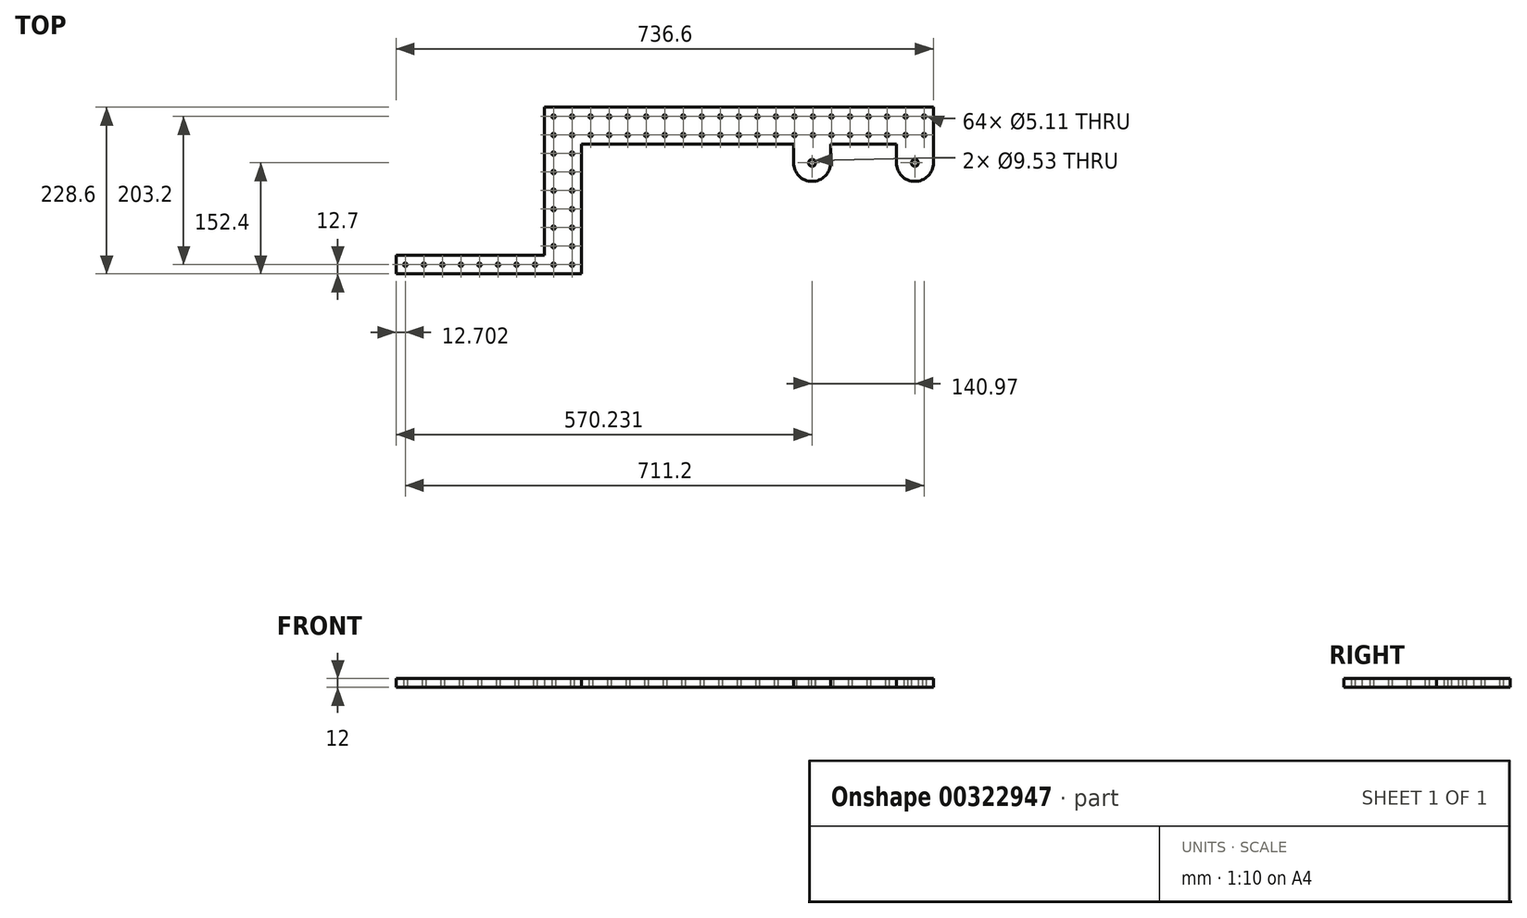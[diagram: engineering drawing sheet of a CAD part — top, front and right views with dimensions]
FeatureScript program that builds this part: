
annotation { "Feature Type Name" : "Feature", "Feature Type Description" : "" }
export const myFeature = defineFeature(function(context is Context, id is Id, definition is map)
    precondition{}
    {
        {
            var Q0;
            Q0=qCreatedBy(makeId("Top.planeOp"),FACE);
            var sketch = newSketch(context, id + "F0", { "sketchPlane" : qUnion([Q0])});
            skLineSegment(sketch, "E0", {"start": v(-259.3, 50.8) * mm, "end": v(274.1, 50.8) * mm});
            skLineSegment(sketch, "E1", {"start": v(274.1, 50.8) * mm, "end": v(274.1, 0) * mm});
            skLineSegment(sketch, "E2", {"start": v(-208.5, -177.8) * mm, "end": v(-208.5, 0) * mm});
            skLineSegment(sketch, "E3", {"start": v(-208.5, 0) * mm, "end": v(82.32, 0) * mm});
            skLineSegment(sketch, "E4", {"start": v(82.32, -25.4) * mm, "end": v(271.56, -25.4) * mm, "construction": true});
            skLineSegment(sketch, "E5", {"start": v(133.12, -25.4) * mm, "end": v(133.12, 0) * mm});
            skLineSegment(sketch, "E6", {"start": v(274.1, 0) * mm, "end": v(274.1, -25.4) * mm});
            skLineSegment(sketch, "E7", {"start": v(223.3, 0) * mm, "end": v(223.3, -25.4) * mm});
            skArc(sketch, "E8", {"start": v(223.3, -25.4) * mm, "mid": v(248.7, -50.8) * mm, "end": v(274.1, -25.4) * mm});
            skLineSegment(sketch, "E9", {"start": v(82.32, 0) * mm, "end": v(82.32, -25.4) * mm});
            skArc(sketch, "E10", {"start": v(82.32, -25.4) * mm, "mid": v(107.72, -50.8) * mm, "end": v(133.12, -25.4) * mm});
            skLineSegment(sketch, "E11", {"start": v(133.12, 0) * mm, "end": v(223.3, 0) * mm});
            skCircle(sketch, "E12", {"center": v(107.72, -25.4) * mm, "radius": 4.76 * mm});
            skCircle(sketch, "E13", {"center": v(248.7, -25.4) * mm, "radius": 4.76 * mm});
            skLineSegment(sketch, "E14", {"start": v(-259.3, 50.8) * mm, "end": v(-259.3, -152.4) * mm});
            skLineSegment(sketch, "E15", {"start": v(-259.3, -152.4) * mm, "end": v(-462.5, -152.4) * mm});
            skLineSegment(sketch, "E16", {"start": v(-462.5, -152.4) * mm, "end": v(-462.5, -177.8) * mm});
            skLineSegment(sketch, "E17", {"start": v(-462.5, -177.8) * mm, "end": v(-208.5, -177.8) * mm});
            skCircle(sketch, "E18", {"center": v(-449.8, -165.1) * mm, "radius": 2.55 * mm});
            skPoint(sketch, "E18.centerSnap0", {"position": v(-462.5, -165.1) * mm});
            skCircle(sketch, "E19.1.0.0", {"center": v(-424.4, -165.1) * mm, "radius": 2.55 * mm});
            skCircle(sketch, "E19.2.0.0", {"center": v(-399, -165.1) * mm, "radius": 2.55 * mm});
            skCircle(sketch, "E19.3.0.0", {"center": v(-373.6, -165.1) * mm, "radius": 2.55 * mm});
            skCircle(sketch, "E19.4.0.0", {"center": v(-348.2, -165.1) * mm, "radius": 2.55 * mm});
            skCircle(sketch, "E19.5.0.0", {"center": v(-322.8, -165.1) * mm, "radius": 2.55 * mm});
            skCircle(sketch, "E19.6.0.0", {"center": v(-297.4, -165.1) * mm, "radius": 2.55 * mm});
            skCircle(sketch, "E19.7.0.0", {"center": v(-272, -165.1) * mm, "radius": 2.55 * mm});
            skLineSegment(sketch, "E19.direction1", {"start": v(-449.8, -165.1) * mm, "end": v(-424.4, -165.1) * mm, "construction": true});
            skCircle(sketch, "E20", {"center": v(-246.6, -165.1) * mm, "radius": 2.55 * mm});
            skCircle(sketch, "E21.0.1.0", {"center": v(-246.6, -139.7) * mm, "radius": 2.55 * mm});
            skCircle(sketch, "E21.0.2.0", {"center": v(-246.6, -114.3) * mm, "radius": 2.55 * mm});
            skCircle(sketch, "E21.0.3.0", {"center": v(-246.6, -88.9) * mm, "radius": 2.55 * mm});
            skCircle(sketch, "E21.0.4.0", {"center": v(-246.6, -63.5) * mm, "radius": 2.55 * mm});
            skCircle(sketch, "E21.0.5.0", {"center": v(-246.6, -38.1) * mm, "radius": 2.55 * mm});
            skCircle(sketch, "E21.0.6.0", {"center": v(-246.6, -12.7) * mm, "radius": 2.55 * mm});
            skCircle(sketch, "E21.0.7.0", {"center": v(-246.6, 12.7) * mm, "radius": 2.55 * mm});
            skCircle(sketch, "E21.0.8.0", {"center": v(-246.6, 38.1) * mm, "radius": 2.55 * mm});
            skCircle(sketch, "E21.1.0.0", {"center": v(-221.2, -165.1) * mm, "radius": 2.55 * mm});
            skCircle(sketch, "E21.1.1.0", {"center": v(-221.2, -139.7) * mm, "radius": 2.55 * mm});
            skCircle(sketch, "E21.1.2.0", {"center": v(-221.2, -114.3) * mm, "radius": 2.55 * mm});
            skCircle(sketch, "E21.1.3.0", {"center": v(-221.2, -88.9) * mm, "radius": 2.55 * mm});
            skCircle(sketch, "E21.1.4.0", {"center": v(-221.2, -63.5) * mm, "radius": 2.55 * mm});
            skCircle(sketch, "E21.1.5.0", {"center": v(-221.2, -38.1) * mm, "radius": 2.55 * mm});
            skCircle(sketch, "E21.1.6.0", {"center": v(-221.2, -12.7) * mm, "radius": 2.55 * mm});
            skCircle(sketch, "E21.1.7.0", {"center": v(-221.2, 12.7) * mm, "radius": 2.55 * mm});
            skCircle(sketch, "E21.1.8.0", {"center": v(-221.2, 38.1) * mm, "radius": 2.55 * mm});
            skLineSegment(sketch, "E21.direction1", {"start": v(-246.6, -165.1) * mm, "end": v(-221.2, -165.1) * mm, "construction": true});
            skLineSegment(sketch, "E21.direction2", {"start": v(-246.6, -165.1) * mm, "end": v(-246.6, -139.7) * mm, "construction": true});
            skLineSegment(sketch, "E22", {"start": v(-208.5, 0) * mm, "end": v(-208.5, 50.8) * mm, "construction": true});
            skCircle(sketch, "E23", {"center": v(-195.8, 12.7) * mm, "radius": 2.55 * mm});
            skCircle(sketch, "E24.0.1.0", {"center": v(-195.8, 38.1) * mm, "radius": 2.55 * mm});
            skCircle(sketch, "E24.1.0.0", {"center": v(-170.4, 12.7) * mm, "radius": 2.55 * mm});
            skCircle(sketch, "E24.1.1.0", {"center": v(-170.4, 38.1) * mm, "radius": 2.55 * mm});
            skCircle(sketch, "E24.2.0.0", {"center": v(-145, 12.7) * mm, "radius": 2.55 * mm});
            skCircle(sketch, "E24.2.1.0", {"center": v(-145, 38.1) * mm, "radius": 2.55 * mm});
            skCircle(sketch, "E24.3.0.0", {"center": v(-119.6, 12.7) * mm, "radius": 2.55 * mm});
            skCircle(sketch, "E24.3.1.0", {"center": v(-119.6, 38.1) * mm, "radius": 2.55 * mm});
            skCircle(sketch, "E24.4.0.0", {"center": v(-94.2, 12.7) * mm, "radius": 2.55 * mm});
            skCircle(sketch, "E24.4.1.0", {"center": v(-94.2, 38.1) * mm, "radius": 2.55 * mm});
            skCircle(sketch, "E24.5.0.0", {"center": v(-68.8, 12.7) * mm, "radius": 2.55 * mm});
            skCircle(sketch, "E24.5.1.0", {"center": v(-68.8, 38.1) * mm, "radius": 2.55 * mm});
            skCircle(sketch, "E24.6.0.0", {"center": v(-43.4, 12.7) * mm, "radius": 2.55 * mm});
            skCircle(sketch, "E24.6.1.0", {"center": v(-43.4, 38.1) * mm, "radius": 2.55 * mm});
            skCircle(sketch, "E24.7.0.0", {"center": v(-18, 12.7) * mm, "radius": 2.55 * mm});
            skCircle(sketch, "E24.7.1.0", {"center": v(-18, 38.1) * mm, "radius": 2.55 * mm});
            skCircle(sketch, "E24.8.0.0", {"center": v(7.4, 12.7) * mm, "radius": 2.55 * mm});
            skCircle(sketch, "E24.8.1.0", {"center": v(7.4, 38.1) * mm, "radius": 2.55 * mm});
            skCircle(sketch, "E24.9.0.0", {"center": v(32.8, 12.7) * mm, "radius": 2.55 * mm});
            skCircle(sketch, "E24.9.1.0", {"center": v(32.8, 38.1) * mm, "radius": 2.55 * mm});
            skCircle(sketch, "E24.10.0.0", {"center": v(58.2, 12.7) * mm, "radius": 2.55 * mm});
            skCircle(sketch, "E24.10.1.0", {"center": v(58.2, 38.1) * mm, "radius": 2.55 * mm});
            skCircle(sketch, "E24.11.0.0", {"center": v(83.6, 12.7) * mm, "radius": 2.55 * mm});
            skCircle(sketch, "E24.11.1.0", {"center": v(83.6, 38.1) * mm, "radius": 2.55 * mm});
            skCircle(sketch, "E24.12.0.0", {"center": v(109, 12.7) * mm, "radius": 2.55 * mm});
            skCircle(sketch, "E24.12.1.0", {"center": v(109, 38.1) * mm, "radius": 2.55 * mm});
            skCircle(sketch, "E24.13.0.0", {"center": v(134.4, 12.7) * mm, "radius": 2.55 * mm});
            skCircle(sketch, "E24.13.1.0", {"center": v(134.4, 38.1) * mm, "radius": 2.55 * mm});
            skCircle(sketch, "E24.14.0.0", {"center": v(159.8, 12.7) * mm, "radius": 2.55 * mm});
            skCircle(sketch, "E24.14.1.0", {"center": v(159.8, 38.1) * mm, "radius": 2.55 * mm});
            skCircle(sketch, "E24.15.0.0", {"center": v(185.2, 12.7) * mm, "radius": 2.55 * mm});
            skCircle(sketch, "E24.15.1.0", {"center": v(185.2, 38.1) * mm, "radius": 2.55 * mm});
            skCircle(sketch, "E24.16.0.0", {"center": v(210.6, 12.7) * mm, "radius": 2.55 * mm});
            skCircle(sketch, "E24.16.1.0", {"center": v(210.6, 38.1) * mm, "radius": 2.55 * mm});
            skCircle(sketch, "E24.17.0.0", {"center": v(236, 12.7) * mm, "radius": 2.55 * mm});
            skCircle(sketch, "E24.17.1.0", {"center": v(236, 38.1) * mm, "radius": 2.55 * mm});
            skCircle(sketch, "E24.18.0.0", {"center": v(261.4, 12.7) * mm, "radius": 2.55 * mm});
            skCircle(sketch, "E24.18.1.0", {"center": v(261.4, 38.1) * mm, "radius": 2.55 * mm});
            skLineSegment(sketch, "E24.direction1", {"start": v(-195.8, 12.7) * mm, "end": v(-170.4, 12.7) * mm, "construction": true});
            skLineSegment(sketch, "E24.direction2", {"start": v(-195.8, 12.7) * mm, "end": v(-195.8, 38.1) * mm, "construction": true});
            skSolve(sketch);
        }
        {
            var Q0;
            Q0=makeQuery(id+"F0.imprint","IMPRINT",FACE,{"disambiguationData":[TD([[makeQuery(id+"F0.imprint","IMPRINT",EDGE,{"derivedFrom":sQuery(id+"F0.wireOp",EDGE,"E0")}),-1.0]])]});
            extrude(context, id + "F1", {"entities" : qUnion([Q0]), "depth" : 12 * mm});
        }
    });
